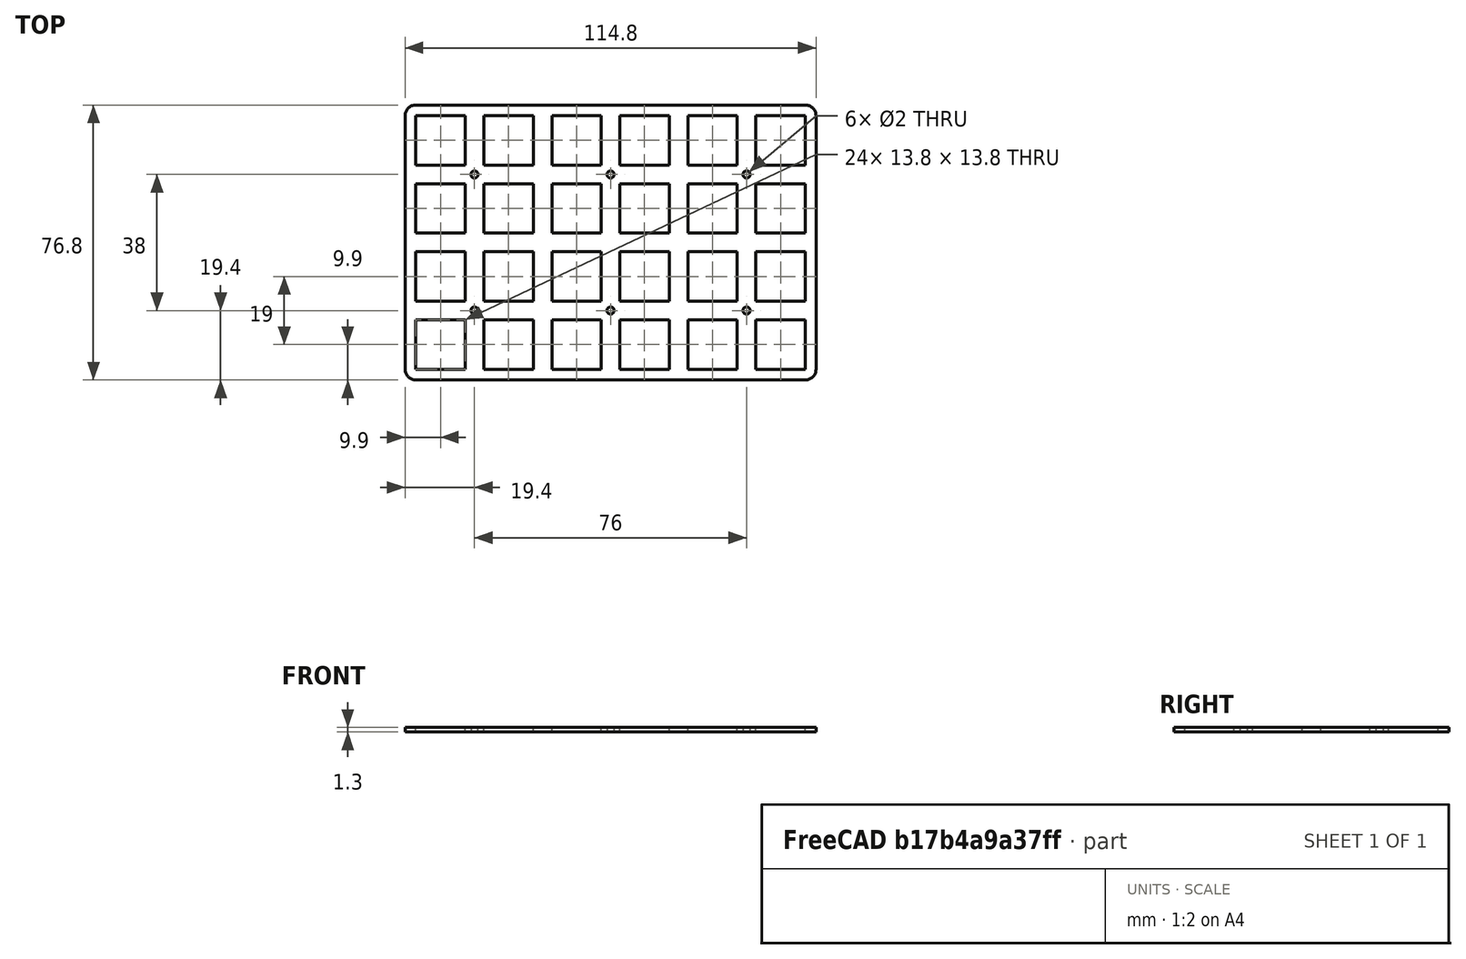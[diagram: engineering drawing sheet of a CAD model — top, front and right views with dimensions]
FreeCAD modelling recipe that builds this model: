
FCSTD DOCUMENT  (FreeCAD 0.18R15860 (Git))
Label: switch mounting plate
License: All rights reserved
LicenseURL: http://en.wikipedia.org/wiki/All_rights_reserved
objects: Sketcher::SketchObject×1, PartDesign::Pad×1, PartDesign::Body×1
note: 4 computed .brp shape members not serialized (recipe doc carries the construction recipe); baked Part::Feature solids carry a one-line shape summary decoded from their .brp

FEATURE [Sketcher::SketchObject] Sketch
  MapMode = 5
  Support = -> [XY_Plane]
  sketch-geometry (122):
    g0: LineSegment StartX=0 StartY=0 StartZ=0 EndX=13.8 EndY=0 EndZ=0
    g1: LineSegment StartX=13.8 StartY=0 StartZ=0 EndX=13.8 EndY=13.8 EndZ=0
    g2: LineSegment StartX=13.8 StartY=13.8 StartZ=0 EndX=0 EndY=13.8 EndZ=0
    g3: LineSegment StartX=0 StartY=13.8 StartZ=0 EndX=0 EndY=0 EndZ=0
    g4: LineSegment StartX=19 StartY=0 StartZ=0 EndX=32.8 EndY=0 EndZ=0
    g5: LineSegment StartX=32.8 StartY=0 StartZ=0 EndX=32.8 EndY=13.8 EndZ=0
    g6: LineSegment StartX=32.8 StartY=13.8 StartZ=0 EndX=19 EndY=13.8 EndZ=0
    g7: LineSegment StartX=19 StartY=13.8 StartZ=0 EndX=19 EndY=0 EndZ=0
    g8: LineSegment StartX=38 StartY=0 StartZ=0 EndX=51.8 EndY=0 EndZ=0
    g9: LineSegment StartX=51.8 StartY=0 StartZ=0 EndX=51.8 EndY=13.8 EndZ=0
    g10: LineSegment StartX=51.8 StartY=13.8 StartZ=0 EndX=38 EndY=13.8 EndZ=0
    g11: LineSegment StartX=38 StartY=13.8 StartZ=0 EndX=38 EndY=0 EndZ=0
    g12: LineSegment StartX=57 StartY=0 StartZ=0 EndX=70.8 EndY=0 EndZ=0
    g13: LineSegment StartX=70.8 StartY=0 StartZ=0 EndX=70.8 EndY=13.8 EndZ=0
    g14: LineSegment StartX=70.8 StartY=13.8 StartZ=0 EndX=57 EndY=13.8 EndZ=0
    g15: LineSegment StartX=57 StartY=13.8 StartZ=0 EndX=57 EndY=0 EndZ=0
    g16: LineSegment StartX=76 StartY=0 StartZ=0 EndX=89.8 EndY=0 EndZ=0
    g17: LineSegment StartX=89.8 StartY=0 StartZ=0 EndX=89.8 EndY=13.8 EndZ=0
    g18: LineSegment StartX=89.8 StartY=13.8 StartZ=0 EndX=76 EndY=13.8 EndZ=0
    g19: LineSegment StartX=76 StartY=13.8 StartZ=0 EndX=76 EndY=0 EndZ=0
    g20: LineSegment StartX=95 StartY=0 StartZ=0 EndX=108.8 EndY=0 EndZ=0
    g21: LineSegment StartX=108.8 StartY=0 StartZ=0 EndX=108.8 EndY=13.8 EndZ=0
    g22: LineSegment StartX=108.8 StartY=13.8 StartZ=0 EndX=95 EndY=13.8 EndZ=0
    g23: LineSegment StartX=95 StartY=13.8 StartZ=0 EndX=95 EndY=0 EndZ=0
    g24: LineSegment StartX=0 StartY=-19 StartZ=0 EndX=13.8 EndY=-19 EndZ=0
    g25: LineSegment StartX=13.8 StartY=-19 StartZ=0 EndX=13.8 EndY=-5.2 EndZ=0
    g26: LineSegment StartX=13.8 StartY=-5.2 StartZ=0 EndX=0 EndY=-5.2 EndZ=0
    g27: LineSegment StartX=0 StartY=-5.2 StartZ=0 EndX=0 EndY=-19 EndZ=0
    g28: LineSegment StartX=19 StartY=-19 StartZ=0 EndX=32.8 EndY=-19 EndZ=0
    g29: LineSegment StartX=32.8 StartY=-19 StartZ=0 EndX=32.8 EndY=-5.2 EndZ=0
    g30: LineSegment StartX=32.8 StartY=-5.2 StartZ=0 EndX=19 EndY=-5.2 EndZ=0
    g31: LineSegment StartX=19 StartY=-5.2 StartZ=0 EndX=19 EndY=-19 EndZ=0
    g32: LineSegment StartX=38 StartY=-19 StartZ=0 EndX=51.8 EndY=-19 EndZ=0
    g33: LineSegment StartX=51.8 StartY=-19 StartZ=0 EndX=51.8 EndY=-5.2 EndZ=0
    g34: LineSegment StartX=51.8 StartY=-5.2 StartZ=0 EndX=38 EndY=-5.2 EndZ=0
    g35: LineSegment StartX=38 StartY=-5.2 StartZ=0 EndX=38 EndY=-19 EndZ=0
    g36: LineSegment StartX=57 StartY=-19 StartZ=0 EndX=70.8 EndY=-19 EndZ=0
    g37: LineSegment StartX=70.8 StartY=-19 StartZ=0 EndX=70.8 EndY=-5.2 EndZ=0
    g38: LineSegment StartX=70.8 StartY=-5.2 StartZ=0 EndX=57 EndY=-5.2 EndZ=0
    g39: LineSegment StartX=57 StartY=-5.2 StartZ=0 EndX=57 EndY=-19 EndZ=0
    g40: LineSegment StartX=76 StartY=-19 StartZ=0 EndX=89.8 EndY=-19 EndZ=0
    g41: LineSegment StartX=89.8 StartY=-19 StartZ=0 EndX=89.8 EndY=-5.2 EndZ=0
    g42: LineSegment StartX=89.8 StartY=-5.2 StartZ=0 EndX=76 EndY=-5.2 EndZ=0
    g43: LineSegment StartX=76 StartY=-5.2 StartZ=0 EndX=76 EndY=-19 EndZ=0
    g44: LineSegment StartX=95 StartY=-19 StartZ=0 EndX=108.8 EndY=-19 EndZ=0
    g45: LineSegment StartX=108.8 StartY=-19 StartZ=0 EndX=108.8 EndY=-5.2 EndZ=0
    g46: LineSegment StartX=108.8 StartY=-5.2 StartZ=0 EndX=95 EndY=-5.2 EndZ=0
    g47: LineSegment StartX=95 StartY=-5.2 StartZ=0 EndX=95 EndY=-19 EndZ=0
    g48: LineSegment StartX=0 StartY=-38 StartZ=0 EndX=13.8 EndY=-38 EndZ=0
    g49: LineSegment StartX=13.8 StartY=-38 StartZ=0 EndX=13.8 EndY=-24.2 EndZ=0
    g50: LineSegment StartX=13.8 StartY=-24.2 StartZ=0 EndX=0 EndY=-24.2 EndZ=0
    g51: LineSegment StartX=0 StartY=-24.2 StartZ=0 EndX=0 EndY=-38 EndZ=0
    g52: LineSegment StartX=19 StartY=-38 StartZ=0 EndX=32.8 EndY=-38 EndZ=0
    g53: LineSegment StartX=32.8 StartY=-38 StartZ=0 EndX=32.8 EndY=-24.2 EndZ=0
    g54: LineSegment StartX=32.8 StartY=-24.2 StartZ=0 EndX=19 EndY=-24.2 EndZ=0
    g55: LineSegment StartX=19 StartY=-24.2 StartZ=0 EndX=19 EndY=-38 EndZ=0
    g56: LineSegment StartX=38 StartY=-38 StartZ=0 EndX=51.8 EndY=-38 EndZ=0
    g57: LineSegment StartX=51.8 StartY=-38 StartZ=0 EndX=51.8 EndY=-24.2 EndZ=0
    g58: LineSegment StartX=51.8 StartY=-24.2 StartZ=0 EndX=38 EndY=-24.2 EndZ=0
    g59: LineSegment StartX=38 StartY=-24.2 StartZ=0 EndX=38 EndY=-38 EndZ=0
    g60: LineSegment StartX=57 StartY=-38 StartZ=0 EndX=70.8 EndY=-38 EndZ=0
    g61: LineSegment StartX=70.8 StartY=-38 StartZ=0 EndX=70.8 EndY=-24.2 EndZ=0
    g62: LineSegment StartX=70.8 StartY=-24.2 StartZ=0 EndX=57 EndY=-24.2 EndZ=0
    g63: LineSegment StartX=57 StartY=-24.2 StartZ=0 EndX=57 EndY=-38 EndZ=0
    g64: LineSegment StartX=76 StartY=-38 StartZ=0 EndX=89.8 EndY=-38 EndZ=0
    g65: LineSegment StartX=89.8 StartY=-38 StartZ=0 EndX=89.8 EndY=-24.2 EndZ=0
    g66: LineSegment StartX=89.8 StartY=-24.2 StartZ=0 EndX=76 EndY=-24.2 EndZ=0
    g67: LineSegment StartX=76 StartY=-24.2 StartZ=0 EndX=76 EndY=-38 EndZ=0
    g68: LineSegment StartX=95 StartY=-38 StartZ=0 EndX=108.8 EndY=-38 EndZ=0
    g69: LineSegment StartX=108.8 StartY=-38 StartZ=0 EndX=108.8 EndY=-24.2 EndZ=0
    g70: LineSegment StartX=108.8 StartY=-24.2 StartZ=0 EndX=95 EndY=-24.2 EndZ=0
    g71: LineSegment StartX=95 StartY=-24.2 StartZ=0 EndX=95 EndY=-38 EndZ=0
    g72: LineSegment StartX=0 StartY=-57 StartZ=0 EndX=13.8 EndY=-57 EndZ=0
    g73: LineSegment StartX=13.8 StartY=-57 StartZ=0 EndX=13.8 EndY=-43.2 EndZ=0
    g74: LineSegment StartX=13.8 StartY=-43.2 StartZ=0 EndX=0 EndY=-43.2 EndZ=0
    g75: LineSegment StartX=0 StartY=-43.2 StartZ=0 EndX=0 EndY=-57 EndZ=0
    g76: LineSegment StartX=19 StartY=-57 StartZ=0 EndX=32.8 EndY=-57 EndZ=0
    g77: LineSegment StartX=32.8 StartY=-57 StartZ=0 EndX=32.8 EndY=-43.2 EndZ=0
    g78: LineSegment StartX=32.8 StartY=-43.2 StartZ=0 EndX=19 EndY=-43.2 EndZ=0
    g79: LineSegment StartX=19 StartY=-43.2 StartZ=0 EndX=19 EndY=-57 EndZ=0
    g80: LineSegment StartX=38 StartY=-57 StartZ=0 EndX=51.8 EndY=-57 EndZ=0
    g81: LineSegment StartX=51.8 StartY=-57 StartZ=0 EndX=51.8 EndY=-43.2 EndZ=0
    g82: LineSegment StartX=51.8 StartY=-43.2 StartZ=0 EndX=38 EndY=-43.2 EndZ=0
    g83: LineSegment StartX=38 StartY=-43.2 StartZ=0 EndX=38 EndY=-57 EndZ=0
    g84: LineSegment StartX=57 StartY=-57 StartZ=0 EndX=70.8 EndY=-57 EndZ=0
    g85: LineSegment StartX=70.8 StartY=-57 StartZ=0 EndX=70.8 EndY=-43.2 EndZ=0
    g86: LineSegment StartX=70.8 StartY=-43.2 StartZ=0 EndX=57 EndY=-43.2 EndZ=0
    g87: LineSegment StartX=57 StartY=-43.2 StartZ=0 EndX=57 EndY=-57 EndZ=0
    g88: LineSegment StartX=76 StartY=-57 StartZ=0 EndX=89.8 EndY=-57 EndZ=0
    g89: LineSegment StartX=89.8 StartY=-57 StartZ=0 EndX=89.8 EndY=-43.2 EndZ=0
    g90: LineSegment StartX=89.8 StartY=-43.2 StartZ=0 EndX=76 EndY=-43.2 EndZ=0
    g91: LineSegment StartX=76 StartY=-43.2 StartZ=0 EndX=76 EndY=-57 EndZ=0
    g92: LineSegment StartX=95 StartY=-57 StartZ=0 EndX=108.8 EndY=-57 EndZ=0
    g93: LineSegment StartX=108.8 StartY=-57 StartZ=0 EndX=108.8 EndY=-43.2 EndZ=0
    g94: LineSegment StartX=108.8 StartY=-43.2 StartZ=0 EndX=95 EndY=-43.2 EndZ=0
    g95: LineSegment StartX=95 StartY=-43.2 StartZ=0 EndX=95 EndY=-57 EndZ=0
    g96: LineSegment [constr] StartX=13.8 StartY=-43.2 StartZ=0 EndX=19 EndY=-38 EndZ=0
    g97: LineSegment [constr] StartX=13.8 StartY=-38 StartZ=0 EndX=19 EndY=-43.2 EndZ=0
    g98: LineSegment [constr] StartX=51.8 StartY=-38 StartZ=0 EndX=57 EndY=-43.2 EndZ=0
    g99: LineSegment [constr] StartX=51.8 StartY=-43.2 StartZ=0 EndX=57 EndY=-38 EndZ=0
    g100: LineSegment [constr] StartX=89.8 StartY=-43.2 StartZ=0 EndX=95 EndY=-38 EndZ=0
    g101: LineSegment [constr] StartX=89.8 StartY=-38 StartZ=0 EndX=95 EndY=-43.2 EndZ=0
    g102: Circle CenterX=92.4 CenterY=-40.6 CenterZ=0 NormalX=0 NormalY=0 NormalZ=1 AngleXU=0 Radius=1
    g103: Circle CenterX=54.4 CenterY=-40.6 CenterZ=0 NormalX=0 NormalY=0 NormalZ=1 AngleXU=0 Radius=1
    g104: Circle CenterX=16.4 CenterY=-40.6 CenterZ=0 NormalX=0 NormalY=0 NormalZ=1 AngleXU=0 Radius=1
    g105: LineSegment [constr] StartX=13.8 StartY=-5.2 StartZ=0 EndX=19 EndY=0 EndZ=0
    g106: LineSegment [constr] StartX=13.8 StartY=0 StartZ=0 EndX=19 EndY=-5.2 EndZ=0
    g107: LineSegment [constr] StartX=51.8 StartY=0 StartZ=0 EndX=57 EndY=-5.2 EndZ=0
    g108: LineSegment [constr] StartX=51.8 StartY=-5.2 StartZ=0 EndX=57 EndY=0 EndZ=0
    g109: LineSegment [constr] StartX=89.8 StartY=0 StartZ=0 EndX=95 EndY=-5.2 EndZ=0
    g110: LineSegment [constr] StartX=89.8 StartY=-5.2 StartZ=0 EndX=95 EndY=0 EndZ=0
    g111: Circle CenterX=16.4 CenterY=-2.6 CenterZ=0 NormalX=0 NormalY=0 NormalZ=1 AngleXU=0 Radius=1
    g112: Circle CenterX=54.4 CenterY=-2.6 CenterZ=0 NormalX=0 NormalY=0 NormalZ=1 AngleXU=0 Radius=1
    g113: Circle CenterX=92.4 CenterY=-2.6 CenterZ=0 NormalX=0 NormalY=0 NormalZ=1 AngleXU=0 Radius=1
    g114: ArcOfCircle CenterX=0 CenterY=13.8 CenterZ=0 NormalX=0 NormalY=0 NormalZ=1 AngleXU=0 Radius=3 StartAngle=1.5708 EndAngle=3.14159
    g115: ArcOfCircle CenterX=108.8 CenterY=13.8 CenterZ=0 NormalX=0 NormalY=0 NormalZ=1 AngleXU=0 Radius=3 StartAngle=0 EndAngle=1.5708
    g116: ArcOfCircle CenterX=108.8 CenterY=-57 CenterZ=0 NormalX=0 NormalY=0 NormalZ=1 AngleXU=0 Radius=3 StartAngle=4.71239 EndAngle=6.28319
    g117: ArcOfCircle CenterX=0 CenterY=-57 CenterZ=0 NormalX=0 NormalY=0 NormalZ=1 AngleXU=0 Radius=3 StartAngle=3.14159 EndAngle=4.71239
    g118: LineSegment StartX=-6e-16 StartY=-60 StartZ=0 EndX=108.8 EndY=-60 EndZ=0
    g119: LineSegment StartX=111.8 StartY=-57 StartZ=0 EndX=111.8 EndY=13.8 EndZ=0
    g120: LineSegment StartX=108.8 StartY=16.8 StartZ=0 EndX=0 EndY=16.8 EndZ=0
    g121: LineSegment StartX=-3 StartY=13.8 StartZ=0 EndX=-3 EndY=-57 EndZ=0
  constraints (355):
    c: Coincident(g0,g1)
    c: Coincident(g1,g2)
    c: Coincident(g2,g3)
    c: Coincident(g3,g0)
    c: Horizontal(g0)
    c: Horizontal(g2)
    c: Vertical(g1)
    c: Vertical(g3)
    c: Coincident(g0,g-1)
    c: Distance(g2) = 13.8
    c: Distance(g3) = 13.8
    c: Coincident(g4,g5)
    c: Coincident(g5,g6)
    c: Coincident(g6,g7)
    c: Coincident(g7,g4)
    c: Horizontal(g4)
    c: Horizontal(g6)
    c: Vertical(g5)
    c: Vertical(g7)
    c: PointOnObject(g4,g-1)
    c: Coincident(g8,g9)
    c: Coincident(g9,g10)
    c: Coincident(g10,g11)
    c: Coincident(g11,g8)
    c: Horizontal(g8)
    c: Horizontal(g10)
    c: Vertical(g9)
    c: Vertical(g11)
    c: PointOnObject(g8,g-1)
    c: Coincident(g12,g13)
    c: Coincident(g13,g14)
    c: Coincident(g14,g15)
    c: Coincident(g15,g12)
    c: Horizontal(g12)
    c: Horizontal(g14)
    c: Vertical(g13)
    c: Vertical(g15)
    c: PointOnObject(g12,g-1)
    c: Coincident(g16,g17)
    c: Coincident(g17,g18)
    c: Coincident(g18,g19)
    c: Coincident(g19,g16)
    c: Horizontal(g16)
    c: Horizontal(g18)
    c: Vertical(g17)
    c: Vertical(g19)
    c: PointOnObject(g16,g-1)
    c: Coincident(g20,g21)
    c: Coincident(g21,g22)
    c: Coincident(g22,g23)
    c: Coincident(g23,g20)
    c: Horizontal(g20)
    c: Horizontal(g22)
    c: Vertical(g21)
    c: Vertical(g23)
    c: PointOnObject(g20,g-1)
    c: Distance(g7) = 13.8
    c: Distance(g6) = 13.8
    c: Distance(g0,g4) = 19
    c: Distance(g10) = 13.8
    c: Distance(g11) = 13.8
    c: Distance(g8,g4) = 19
    c: Distance(g15) = 13.8
    c: Distance(g14) = 13.8
    c: Distance(g12,g8) = 19
    c: Distance(g19) = 13.8
    c: Distance(g18) = 13.8
    c: Distance(g16,g12) = 19
    c: Distance(g23) = 13.8
    c: Distance(g22) = 13.8
    c: Distance(g20,g16) = 19
    c: Coincident(g24,g25)
    c: Coincident(g25,g26)
    c: Coincident(g26,g27)
    c: Coincident(g27,g24)
    c: Horizontal(g24)
    c: Horizontal(g26)
    c: Vertical(g25)
    c: Vertical(g27)
    c: Equal(g2,g26) = 13.8
    c: Equal(g3,g27) = 13.8
    c: Coincident(g28,g29)
    c: Coincident(g29,g30)
    c: Coincident(g30,g31)
    c: Coincident(g31,g28)
    c: Horizontal(g28)
    c: Horizontal(g30)
    c: Vertical(g29)
    c: Vertical(g31)
    c: Coincident(g32,g33)
    c: Coincident(g33,g34)
    c: Coincident(g34,g35)
    c: Coincident(g35,g32)
    c: Horizontal(g32)
    c: Horizontal(g34)
    c: Vertical(g33)
    c: Vertical(g35)
    c: Coincident(g36,g37)
    c: Coincident(g37,g38)
    c: Coincident(g38,g39)
    c: Coincident(g39,g36)
    c: Horizontal(g36)
    c: Horizontal(g38)
    c: Vertical(g37)
    c: Vertical(g39)
    c: Coincident(g40,g41)
    c: Coincident(g41,g42)
    c: Coincident(g42,g43)
    c: Coincident(g43,g40)
    c: Horizontal(g40)
    c: Horizontal(g42)
    c: Vertical(g41)
    c: Vertical(g43)
    c: Coincident(g44,g45)
    c: Coincident(g45,g46)
    c: Coincident(g46,g47)
    c: Coincident(g47,g44)
    c: Horizontal(g44)
    c: Horizontal(g46)
    c: Vertical(g45)
    c: Vertical(g47)
    c: Equal(g7,g31) = 13.8
    c: Equal(g6,g30) = 13.8
    c: Distance(g24,g28) = 19
    c: Equal(g10,g34) = 13.8
    c: Equal(g11,g35) = 13.8
    c: Distance(g32,g28) = 19
    c: Equal(g15,g39) = 13.8
    c: Equal(g14,g38) = 13.8
    c: Distance(g36,g32) = 19
    c: Equal(g19,g43) = 13.8
    c: Equal(g18,g42) = 13.8
    c: Distance(g40,g36) = 19
    c: Equal(g23,g47) = 13.8
    c: Equal(g22,g46) = 13.8
    c: Distance(g44,g40) = 19
    c: Horizontal(g26,g30)
    c: Horizontal(g29,g34)
    c: Horizontal(g33,g38)
    c: Horizontal(g37,g42)
    c: Horizontal(g41,g46)
    c: PointOnObject(g26,g-2)
    c: Distance(g26,g2) = 19
    c: Coincident(g48,g49)
    c: Coincident(g49,g50)
    c: Coincident(g50,g51)
    c: Coincident(g51,g48)
    c: Horizontal(g48)
    c: Horizontal(g50)
    c: Vertical(g49)
    c: Vertical(g51)
    c: Coincident(g52,g53)
    c: Coincident(g53,g54)
    c: Coincident(g54,g55)
    c: Coincident(g55,g52)
    c: Horizontal(g52)
    c: Horizontal(g54)
    c: Vertical(g53)
    c: Vertical(g55)
    c: Coincident(g56,g57)
    c: Coincident(g57,g58)
    c: Coincident(g58,g59)
    c: Coincident(g59,g56)
    c: Horizontal(g56)
    c: Horizontal(g58)
    c: Vertical(g57)
    c: Vertical(g59)
    c: Coincident(g60,g61)
    c: Coincident(g61,g62)
    c: Coincident(g62,g63)
    c: Coincident(g63,g60)
    c: Horizontal(g60)
    c: Horizontal(g62)
    c: Vertical(g61)
    c: Vertical(g63)
    c: Coincident(g64,g65)
    c: Coincident(g65,g66)
    c: Coincident(g66,g67)
    c: Coincident(g67,g64)
    c: Horizontal(g64)
    c: Horizontal(g66)
    c: Vertical(g65)
    c: Vertical(g67)
    c: Coincident(g68,g69)
    c: Coincident(g69,g70)
    c: Coincident(g70,g71)
    c: Coincident(g71,g68)
    c: Horizontal(g68)
    c: Horizontal(g70)
    c: Vertical(g69)
    c: Vertical(g71)
    c: Distance(g48,g52) = 19
    c: Distance(g56,g52) = 19
    c: Distance(g60,g56) = 19
    c: Distance(g64,g60) = 19
    c: Distance(g68,g64) = 19
    c: Horizontal(g50,g54)
    c: Horizontal(g53,g58)
    c: Horizontal(g57,g62)
    c: Horizontal(g61,g66)
    c: Horizontal(g65,g70)
    c: PointOnObject(g50,g-2)
    c: Distance(g50,g26) = 19
    c: Distance(g51) = 13.8
    c: Horizontal(g52,g48)
    c: Horizontal(g52,g56)
    c: Horizontal(g56,g60)
    c: Horizontal(g60,g64)
    c: Horizontal(g64,g68)
    c: Distance(g58) = 13.8
    c: Distance(g54) = 13.8
    c: Distance(g62) = 13.8
    c: Distance(g66) = 13.8
    c: Distance(g70) = 13.8
    c: Distance(g50) = 13.8
    c: Coincident(g72,g73)
    c: Coincident(g73,g74)
    c: Coincident(g74,g75)
    c: Coincident(g75,g72)
    c: Horizontal(g72)
    c: Horizontal(g74)
    c: Vertical(g73)
    c: Vertical(g75)
    c: Coincident(g76,g77)
    c: Coincident(g77,g78)
    c: Coincident(g78,g79)
    c: Coincident(g79,g76)
    c: Horizontal(g76)
    c: Horizontal(g78)
    c: Vertical(g77)
    c: Vertical(g79)
    c: Coincident(g80,g81)
    c: Coincident(g81,g82)
    c: Coincident(g82,g83)
    c: Coincident(g83,g80)
    c: Horizontal(g80)
    c: Horizontal(g82)
    c: Vertical(g81)
    c: Vertical(g83)
    c: Coincident(g84,g85)
    c: Coincident(g85,g86)
    c: Coincident(g86,g87)
    c: Coincident(g87,g84)
    c: Horizontal(g84)
    c: Horizontal(g86)
    c: Vertical(g85)
    c: Vertical(g87)
    c: Coincident(g88,g89)
    c: Coincident(g89,g90)
    c: Coincident(g90,g91)
    c: Coincident(g91,g88)
    c: Horizontal(g88)
    c: Horizontal(g90)
    c: Vertical(g89)
    c: Vertical(g91)
    c: Coincident(g92,g93)
    c: Coincident(g93,g94)
    c: Coincident(g94,g95)
    c: Coincident(g95,g92)
    c: Horizontal(g92)
    c: Horizontal(g94)
    c: Vertical(g93)
    c: Vertical(g95)
    c: Distance(g72,g76) = 19
    c: Distance(g80,g76) = 19
    c: Distance(g84,g80) = 19
    c: Distance(g88,g84) = 19
    c: Distance(g92,g88) = 19
    c: Horizontal(g74,g78)
    c: Horizontal(g77,g82)
    c: Horizontal(g81,g86)
    c: Horizontal(g85,g90)
    c: Horizontal(g89,g94)
    c: Equal(g51,g75) = 13.8
    c: Horizontal(g76,g72)
    c: Horizontal(g76,g80)
    c: Horizontal(g80,g84)
    c: Horizontal(g84,g88)
    c: Horizontal(g88,g92)
    c: Equal(g58,g82) = 13.8
    c: Equal(g54,g78) = 13.8
    c: Equal(g62,g86) = 13.8
    c: Equal(g66,g90) = 13.8
    c: Equal(g70,g94) = 13.8
    c: Equal(g50,g74) = 13.8
    c: PointOnObject(g74,g-2)
    c: Distance(g74,g50) = 19
    c: Coincident(g96,g73)
    c: Coincident(g96,g52)
    c: Coincident(g97,g48)
    c: Coincident(g97,g78)
    c: Coincident(g98,g56)
    c: Coincident(g98,g86)
    c: Coincident(g99,g81)
    c: Coincident(g99,g60)
    c: Coincident(g100,g89)
    c: Coincident(g100,g68)
    c: Coincident(g101,g64)
    c: Coincident(g101,g94)
    c: PointOnObject(g102,g100)
    c: PointOnObject(g103,g99)
    c: PointOnObject(g104,g96)
    c: Diameter(g104) = 2
    c: Diameter(g103) = 2
    c: Diameter(g102) = 2
    c: PointOnObject(g103,g98)
    c: PointOnObject(g104,g97)
    c: PointOnObject(g102,g101)
    c: Coincident(g105,g25)
    c: Coincident(g105,g4)
    c: Coincident(g106,g0)
    c: Coincident(g106,g30)
    c: Coincident(g107,g8)
    c: Coincident(g107,g38)
    c: Coincident(g108,g33)
    c: Coincident(g108,g12)
    c: Coincident(g109,g16)
    c: Coincident(g109,g46)
    c: Coincident(g110,g41)
    c: Coincident(g110,g20)
    c: PointOnObject(g111,g105)
    c: PointOnObject(g112,g108)
    c: PointOnObject(g113,g110)
    c: Diameter(g111) = 2
    c: Diameter(g112) = 2
    c: Diameter(g113) = 2
    c: PointOnObject(g111,g106)
    c: PointOnObject(g112,g107)
    c: PointOnObject(g113,g109)
    c: Coincident(g114,g2)
    c: PointOnObject(g114,g-2)
    c: Horizontal(g114,g2)
    c: Coincident(g115,g21)
    c: Vertical(g115,g21)
    c: Horizontal(g21,g22)
    c: Horizontal(g22,g115)
    c: Horizontal(g115,g115)
    c: Radius(g115) = 3
    c: Coincident(g116,g92)
    c: Horizontal(g116,g92)
    c: Vertical(g92,g116)
    c: Coincident(g117,g72)
    c: PointOnObject(g117,g-2)
    c: Horizontal(g117,g72)
    c: Radius(g117) = 3
    c: Coincident(g118,g117)
    c: Horizontal(g118)
    c: Coincident(g116,g118)
    c: Coincident(g119,g116)
    c: Coincident(g119,g115)
    c: Coincident(g120,g115)
    c: Coincident(g120,g114)
    c: Horizontal(g120)
    c: Coincident(g121,g114)
    c: Coincident(g121,g117)
FEATURE [PartDesign::Pad] Pad
  Length = 1.3
  Length2 = 100
  Profile = -> Sketch
  Type = 0
FEATURE [PartDesign::Body] Body
  Group = -> [Sketch,Pad]
  Origin = -> Origin
  Tip = -> Pad
